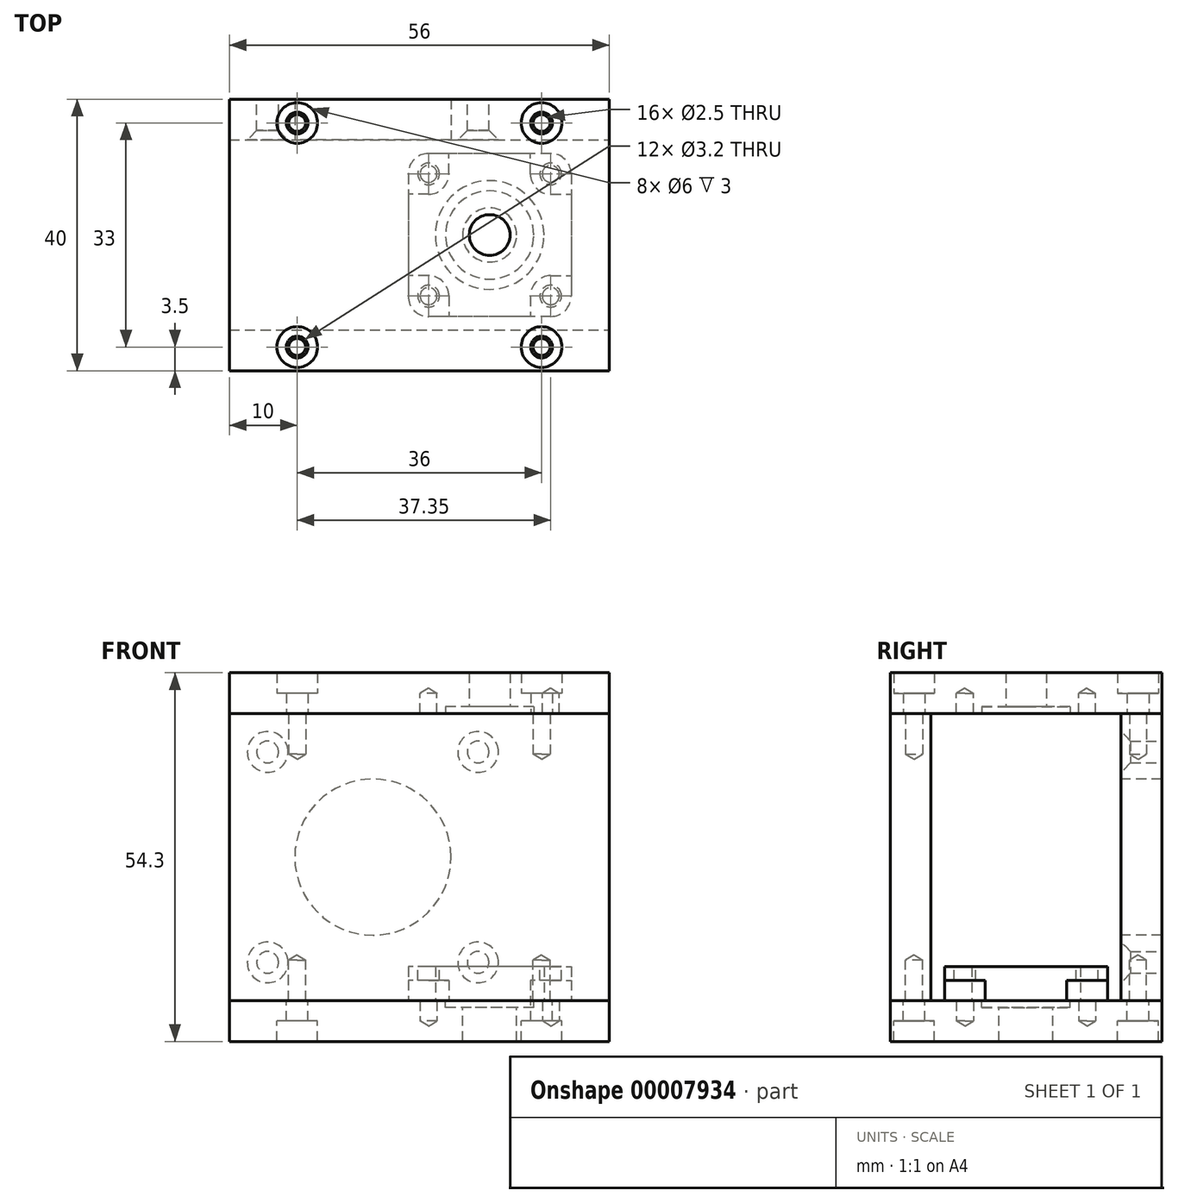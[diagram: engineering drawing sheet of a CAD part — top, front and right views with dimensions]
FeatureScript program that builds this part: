
annotation { "Feature Type Name" : "Feature", "Feature Type Description" : "" }
export const myFeature = defineFeature(function(context is Context, id is Id, definition is map)
    precondition{}
    {
        {
            var Q0;
            Q0=qCreatedBy(makeId("Top.planeOp"),FACE);
            var sketch = newSketch(context, id + "F0", { "sketchPlane" : qUnion([Q0])});
            skLineSegment(sketch, "E0.rect.bottom", {"start": v(-28, 21.15) * mm, "end": v(28, 21.15) * mm});
            skLineSegment(sketch, "E0.rect.top", {"start": v(-28, -21.15) * mm, "end": v(28, -21.15) * mm});
            skLineSegment(sketch, "E0.rect.left", {"start": v(-28, 21.15) * mm, "end": v(-28, -21.15) * mm});
            skLineSegment(sketch, "E0.rect.right", {"start": v(28, 21.15) * mm, "end": v(28, -21.15) * mm});
            skPoint(sketch, "E0.rect.middle", {"position": v(0, 0) * mm});
            skCircle(sketch, "E1", {"center": v(-6.85, 0) * mm, "radius": 11.5 * mm});
            skLineSegment(sketch, "E2", {"start": v(0, 36.49) * mm, "end": v(0, -29.8) * mm, "construction": true});
            skPoint(sketch, "E3", {"position": v(8.65, -15.5) * mm});
            skPoint(sketch, "E4", {"position": v(8.65, 15.5) * mm});
            skPoint(sketch, "E5", {"position": v(-22.35, -15.5) * mm});
            skPoint(sketch, "E6", {"position": v(-22.35, 15.5) * mm});
            skSolve(sketch);
        }
        {
            var Q0;
            Q0=makeQuery(id+"F0.imprint","IMPRINT",FACE,{"disambiguationData":[TD([[makeQuery(id+"F0.imprint","IMPRINT",EDGE,{"derivedFrom":sQuery(id+"F0.wireOp",EDGE,"E0.rect.bottom")}),-1.0]])]});
            extrude(context, id + "F1", {"entities" : qUnion([Q0]), "depth" : 6 * mm});
        }
        {
            var Q0;
            Q0=makeQuery(id+"F1.opExtrude","SWEPT_BODY",BODY,{"disambiguationData":[OSD([sQuery(id+"F0.wireOp",EDGE,"E0.rect.bottom"),sQuery(id+"F0.wireOp",EDGE,"E0.rect.top"),sQuery(id+"F0.wireOp",EDGE,"E0.rect.left"),sQuery(id+"F0.wireOp",EDGE,"E0.rect.right"),sQuery(id+"F0.wireOp",EDGE,"5d0100cf-7879-4639-aec2-40528bfa14ef"),sQuery(id+"F0.wireOp",EDGE,"8731b84f-5775-4f98-9a93-eaf35cf7c801"),sQuery(id+"F0.wireOp",EDGE,"47f3dff2-6889-448c-bae9-9e021a76fb31"),sQuery(id+"F0.wireOp",EDGE,"358dfb72-d0fd-4f4f-ac3b-25c96c6351ab"),sQuery(id+"F0.wireOp",EDGE,"E1")])]});
            var Q1;
            Q1=sQuery(id+"F0.wireOp",EDGE,"E0.rect.bottom");
            var Q2;
            Q2=sQuery(id+"F0.wireOp",EDGE,"E0.rect.bottom");
            transform(context, id + "F2", {"entities" : qUnion([Q0]), "transformType" : TransformType.ROTATION, "transformAxis" : qUnion([Q2]), "angle" : 90 * degree, "oppositeDirection" : true, "makeCopy" : false});
        }
        {
            var Q0;
            Q0=qCreatedBy(makeId("Top.planeOp"),FACE);
            var sketch = newSketch(context, id + "F3", { "sketchPlane" : qUnion([Q0])});
            skLineSegment(sketch, "E7.bottom", {"start": v(-28, 27.15) * mm, "end": v(28, 27.15) * mm});
            skLineSegment(sketch, "E7.top", {"start": v(-28, -12.85) * mm, "end": v(28, -12.85) * mm});
            skLineSegment(sketch, "E7.left", {"start": v(-28, 27.15) * mm, "end": v(-28, -12.85) * mm});
            skLineSegment(sketch, "E7.right", {"start": v(28, 27.15) * mm, "end": v(28, -12.85) * mm});
            skLineSegment(sketch, "E8", {"start": v(-6.85, 27.15) * mm, "end": v(-6.85, -12.85) * mm, "construction": true});
            skLineSegment(sketch, "E9", {"start": v(10.35, 27.15) * mm, "end": v(10.35, -12.85) * mm, "construction": true});
            skLineSegment(sketch, "E10", {"start": v(10.35, -7.18) * mm, "end": v(-6.85, -7.18) * mm, "construction": true});
            skCircle(sketch, "E11", {"center": v(10.35, 7.15) * mm, "radius": 6.5 * mm});
            skSolve(sketch);
        }
        {
            var Q0;
            Q0=makeQuery(id+"F3.imprint","IMPRINT",FACE,{"disambiguationData":[TD([[makeQuery(id+"F3.imprint","IMPRINT",EDGE,{"derivedFrom":sQuery(id+"F3.wireOp",EDGE,"E7.bottom")}),-1.0]])]});
            var Q1;
            Q1=makeQuery(id+"F3.imprint","IMPRINT",FACE,{"disambiguationData":[TD([[makeQuery(id+"F3.imprint","IMPRINT",EDGE,{"derivedFrom":sQuery(id+"F3.wireOp",EDGE,"E11")}),1.0]])]});
            extrude(context, id + "F4", {"entities" : qUnion([Q0, Q1]), "oppositeDirection" : true, "depth" : 6 * mm});
        }
        {
            var Q0;
            Q0=makeQuery(id+"F4.opExtrude","SWEPT_FACE",FACE,{"disambiguationData":[OSD([sQuery(id+"F3.wireOp",EDGE,"E7.top")])]});
            var sketch = newSketch(context, id + "F5", { "sketchPlane" : qUnion([Q0])});
            skLineSegment(sketch, "E12.bottom", {"start": v(-28, 42.3) * mm, "end": v(28, 42.3) * mm});
            skLineSegment(sketch, "E12.top", {"start": v(-28, 0) * mm, "end": v(28, 0) * mm});
            skLineSegment(sketch, "E12.left", {"start": v(28, 42.3) * mm, "end": v(28, 0) * mm});
            skLineSegment(sketch, "E12.right", {"start": v(-28, 42.3) * mm, "end": v(-28, 0) * mm});
            skSolve(sketch);
        }
        {
            var Q0;
            Q0=makeQuery(id+"F5.imprint","IMPRINT",FACE,{"disambiguationData":[TD([[makeQuery(id+"F5.imprint","IMPRINT",EDGE,{"derivedFrom":sQuery(id+"F5.wireOp",EDGE,"E12.bottom")}),-1.0]])]});
            extrude(context, id + "F6", {"entities" : qUnion([Q0]), "oppositeDirection" : true, "depth" : 6 * mm});
        }
        {
            var Q0;
            Q0=makeQuery(id+"F3.imprint","IMPRINT",FACE,{"disambiguationData":[TD([[makeQuery(id+"F3.imprint","IMPRINT",EDGE,{"derivedFrom":sQuery(id+"F3.wireOp",EDGE,"E11")}),1.0]])]});
            extrude(context, id + "F7", {"entities" : qUnion([Q0]), "operationType" : NewBodyOperationType.REMOVE, "oppositeDirection" : true, "depth" : 1 * mm});
        }
        {
            var Q0;
            Q0=makeQuery(id+"F6.opExtrude","SWEPT_FACE",FACE,{"disambiguationData":[OSD([sQuery(id+"F5.wireOp",EDGE,"E12.bottom")])]});
            var sketch = newSketch(context, id + "F8", { "sketchPlane" : qUnion([Q0])});
            skPoint(sketch, "E13.0", {"position": v(10.35, 7.15) * mm});
            skLineSegment(sketch, "E14.0", {"start": v(-28, 27.15) * mm, "end": v(28, 27.15) * mm});
            skLineSegment(sketch, "E15.0", {"start": v(28, 27.15) * mm, "end": v(28, -12.85) * mm});
            skLineSegment(sketch, "E16.0", {"start": v(-28, -12.85) * mm, "end": v(28, -12.85) * mm});
            skLineSegment(sketch, "E17.0", {"start": v(-28, 27.15) * mm, "end": v(-28, -12.85) * mm});
            skCircle(sketch, "E18", {"center": v(10.35, 7.15) * mm, "radius": 3 * mm});
            skCircle(sketch, "E19.0", {"center": v(10.35, 7.15) * mm, "radius": 6.5 * mm});
            skSolve(sketch);
        }
        {
            var Q0;
            Q0=makeQuery(id+"F8.imprint","IMPRINT",FACE,{"disambiguationData":[TD([[makeQuery(id+"F8.imprint","IMPRINT",EDGE,{"derivedFrom":sQuery(id+"F8.wireOp",EDGE,"E18")}),-1.0]])]});
            var Q1;
            {var subQ2=sQuery(id+"F8.wireOp",EDGE,"E14.0");Q1=makeQuery(id+"F8.imprint","IMPRINT",FACE,{"disambiguationData":[TD([[makeQuery(id+"F8.imprint","IMPRINT",EDGE,{"derivedFrom":subQ2}),-1.0]])]});}
            var Q2;
            {var subQ2=sQuery(id+"F8.wireOp",EDGE,"E16.0");Q2=makeQuery(id+"F8.imprint","IMPRINT",FACE,{"disambiguationData":[TD([[makeQuery(id+"F8.imprint","IMPRINT",EDGE,{"derivedFrom":subQ2}),1.0]])]});}
            extrude(context, id + "F9", {"entities" : qUnion([Q0, Q1, Q2]), "depth" : 6 * mm});
        }
        {
            var Q0;
            Q0=makeQuery(id+"F8.imprint","IMPRINT",FACE,{"disambiguationData":[TD([[makeQuery(id+"F8.imprint","IMPRINT",EDGE,{"derivedFrom":sQuery(id+"F8.wireOp",EDGE,"E18")}),-1.0]])]});
            extrude(context, id + "F10", {"entities" : qUnion([Q0]), "operationType" : NewBodyOperationType.REMOVE, "depth" : 1 * mm});
        }
        {
            var Q0;
            Q0=makeQuery(id+"F4.opExtrude","CAP_FACE",FACE,{"disambiguationData":[OSD([sQuery(id+"F3.wireOp",EDGE,"E7.bottom"),sQuery(id+"F3.wireOp",EDGE,"E7.top"),sQuery(id+"F3.wireOp",EDGE,"E7.left"),sQuery(id+"F3.wireOp",EDGE,"E7.right"),sQuery(id+"F3.wireOp",EDGE,"f328e42c-5cb5-4c08-ae33-e700e0f09d0d")])],"isStart":true});
            var sketch = newSketch(context, id + "F11", { "sketchPlane" : qUnion([Q0])});
            skCircle(sketch, "E20", {"center": v(19.35, -1.85) * mm, "radius": 3 * mm});
            skCircle(sketch, "E21", {"center": v(1.35, 16.15) * mm, "radius": 3 * mm});
            skCircle(sketch, "E22", {"center": v(19.35, 16.15) * mm, "radius": 3 * mm});
            skCircle(sketch, "E23", {"center": v(1.35, -1.85) * mm, "radius": 3 * mm});
            skLineSegment(sketch, "E24", {"start": v(19.35, -1.85) * mm, "end": v(22.35, -1.85) * mm, "construction": true});
            skLineSegment(sketch, "E25", {"start": v(19.35, -1.85) * mm, "end": v(19.35, -4.85) * mm, "construction": true});
            skPoint(sketch, "E26.0", {"position": v(10.35, 7.15) * mm});
            skCircle(sketch, "E27", {"center": v(10.35, 7.15) * mm, "radius": 8 * mm});
            skLineSegment(sketch, "E28.rect.bottom", {"start": v(22.35, 19.15) * mm, "end": v(-1.65, 19.15) * mm});
            skLineSegment(sketch, "E28.rect.top", {"start": v(22.35, -4.85) * mm, "end": v(-1.65, -4.85) * mm});
            skLineSegment(sketch, "E28.rect.left", {"start": v(22.35, 19.15) * mm, "end": v(22.35, -4.85) * mm});
            skLineSegment(sketch, "E28.rect.right", {"start": v(-1.65, 19.15) * mm, "end": v(-1.65, -4.85) * mm});
            skLineSegment(sketch, "E29", {"start": v(1.35, 13.15) * mm, "end": v(-1.65, 13.15) * mm});
            skLineSegment(sketch, "E30", {"start": v(22.35, 7.15) * mm, "end": v(-1.65, 7.15) * mm, "construction": true});
            skLineSegment(sketch, "E31", {"start": v(10.35, 19.15) * mm, "end": v(10.35, -4.85) * mm, "construction": true});
            skLineSegment(sketch, "E32", {"start": v(4.35, 16.15) * mm, "end": v(4.35, 19.15) * mm});
            skLineSegment(sketch, "E33", {"start": v(4.35, -1.85) * mm, "end": v(4.35, -4.85) * mm});
            skLineSegment(sketch, "E34", {"start": v(1.35, 1.15) * mm, "end": v(-1.65, 1.15) * mm});
            skLineSegment(sketch, "E35", {"start": v(16.35, 16.15) * mm, "end": v(16.35, 19.15) * mm});
            skLineSegment(sketch, "E36", {"start": v(19.35, 13.15) * mm, "end": v(22.35, 13.15) * mm});
            skLineSegment(sketch, "E37", {"start": v(16.35, -1.85) * mm, "end": v(16.35, -4.85) * mm});
            skLineSegment(sketch, "E38", {"start": v(19.35, 1.15) * mm, "end": v(22.35, 1.15) * mm});
            skSolve(sketch);
        }
        {
            var Q0;
            Q0=makeQuery(id+"F11.imprint","IMPRINT",FACE,{"disambiguationData":[TD([[makeQuery(id+"F11.imprint","IMPRINT",EDGE,{"derivedFrom":sQuery(id+"F11.wireOp",EDGE,"E27")}),-1.0]])]});
            var Q1;
            {var subQ0=sQuery(id+"F11.wireOp",EDGE,"E23");var subQ2=makeQuery(id+"F11.imprint","INTERSECT",VERTEX,{"derivedFrom":[subQ0,sQuery(id+"F11.wireOp",EDGE,"E33")]});Q1=makeQuery(id+"F11.imprint","IMPRINT",FACE,{"disambiguationData":[TD([[makeQuery(id+"F11.imprint","IMPRINT",EDGE,{"disambiguationData":[TD([[subQ2,-1.0]])],"derivedFrom":subQ0}),1.0]])]});}
            var Q2;
            {var subQ0=sQuery(id+"F11.wireOp",EDGE,"E34");Q2=makeQuery(id+"F11.imprint","IMPRINT",FACE,{"disambiguationData":[TD([[makeQuery(id+"F11.imprint","IMPRINT",EDGE,{"derivedFrom":subQ0}),1.0]])]});}
            var Q3;
            {var subQ0=sQuery(id+"F11.wireOp",EDGE,"E33");Q3=makeQuery(id+"F11.imprint","IMPRINT",FACE,{"disambiguationData":[TD([[makeQuery(id+"F11.imprint","IMPRINT",EDGE,{"derivedFrom":subQ0}),-1.0]])]});}
            var Q4;
            {var subQ0=sQuery(id+"F11.wireOp",EDGE,"E32");Q4=makeQuery(id+"F11.imprint","IMPRINT",FACE,{"disambiguationData":[TD([[makeQuery(id+"F11.imprint","IMPRINT",EDGE,{"derivedFrom":subQ0}),1.0]])]});}
            var Q5;
            {var subQ0=sQuery(id+"F11.wireOp",EDGE,"E21");var subQ4=makeQuery(id+"F11.imprint","INTERSECT",VERTEX,{"derivedFrom":[subQ0,sQuery(id+"F11.wireOp",EDGE,"E28.rect.right")]});Q5=makeQuery(id+"F11.imprint","IMPRINT",FACE,{"disambiguationData":[TD([[makeQuery(id+"F11.imprint","IMPRINT",EDGE,{"disambiguationData":[TD([[subQ4,1.0]])],"derivedFrom":subQ0}),1.0]])]});}
            var Q6;
            {var subQ0=sQuery(id+"F11.wireOp",EDGE,"E29");Q6=makeQuery(id+"F11.imprint","IMPRINT",FACE,{"disambiguationData":[TD([[makeQuery(id+"F11.imprint","IMPRINT",EDGE,{"derivedFrom":subQ0}),-1.0]])]});}
            var Q7;
            {var subQ3=sQuery(id+"F11.wireOp",EDGE,"E35");Q7=makeQuery(id+"F11.imprint","IMPRINT",FACE,{"disambiguationData":[TD([[makeQuery(id+"F11.imprint","IMPRINT",EDGE,{"derivedFrom":subQ3}),-1.0]])]});}
            var Q8;
            {var subQ0=sQuery(id+"F11.wireOp",EDGE,"E22");var subQ4=makeQuery(id+"F11.imprint","INTERSECT",VERTEX,{"derivedFrom":[subQ0,sQuery(id+"F11.wireOp",EDGE,"E35")]});Q8=makeQuery(id+"F11.imprint","IMPRINT",FACE,{"disambiguationData":[TD([[makeQuery(id+"F11.imprint","IMPRINT",EDGE,{"disambiguationData":[TD([[subQ4,1.0]])],"derivedFrom":subQ0}),1.0]])]});}
            var Q9;
            {var subQ0=sQuery(id+"F11.wireOp",EDGE,"E36");Q9=makeQuery(id+"F11.imprint","IMPRINT",FACE,{"disambiguationData":[TD([[makeQuery(id+"F11.imprint","IMPRINT",EDGE,{"derivedFrom":subQ0}),1.0]])]});}
            var Q10;
            {var subQ0=sQuery(id+"F11.wireOp",EDGE,"E38");Q10=makeQuery(id+"F11.imprint","IMPRINT",FACE,{"disambiguationData":[TD([[makeQuery(id+"F11.imprint","IMPRINT",EDGE,{"derivedFrom":subQ0}),-1.0]])]});}
            var Q11;
            {var subQ0=sQuery(id+"F11.wireOp",EDGE,"E20");var subQ4=makeQuery(id+"F11.imprint","INTERSECT",VERTEX,{"derivedFrom":[subQ0,sQuery(id+"F11.wireOp",EDGE,"E38")]});Q11=makeQuery(id+"F11.imprint","IMPRINT",FACE,{"disambiguationData":[TD([[makeQuery(id+"F11.imprint","IMPRINT",EDGE,{"disambiguationData":[TD([[subQ4,1.0]])],"derivedFrom":subQ0}),1.0]])]});}
            var Q12;
            {var subQ0=sQuery(id+"F11.wireOp",EDGE,"E37");Q12=makeQuery(id+"F11.imprint","IMPRINT",FACE,{"disambiguationData":[TD([[makeQuery(id+"F11.imprint","IMPRINT",EDGE,{"derivedFrom":subQ0}),1.0]])]});}
            extrude(context, id + "F12", {"entities" : qUnion([Q0, Q1, Q2, Q3, Q4, Q5, Q6, Q7, Q8, Q9, Q10, Q11, Q12]), "depth" : 5 * mm});
        }
        {
            var Q0;
            Q0=sQuery(id+"F11.wireOp",VERTEX,"E21.center");
            var Q1;
            Q1=sQuery(id+"F11.wireOp",VERTEX,"E23.center");
            var Q2;
            Q2=sQuery(id+"F11.wireOp",VERTEX,"E20.center");
            var Q3;
            Q3=sQuery(id+"F11.wireOp",VERTEX,"E22.center");
            var Q4;
            Q4=makeQuery(id+"F12.opExtrude","SWEPT_BODY",BODY,{"disambiguationData":[OSD([sQuery(id+"F11.wireOp",EDGE,"E20"),sQuery(id+"F11.wireOp",EDGE,"E21"),sQuery(id+"F11.wireOp",EDGE,"E22"),sQuery(id+"F11.wireOp",EDGE,"E23"),sQuery(id+"F11.wireOp",EDGE,"E27"),sQuery(id+"F11.wireOp",EDGE,"E28.rect.bottom"),sQuery(id+"F11.wireOp",EDGE,"E28.rect.top"),sQuery(id+"F11.wireOp",EDGE,"E28.rect.left"),sQuery(id+"F11.wireOp",EDGE,"E28.rect.right")])]});
            hole(context, id + "F13", {"style" : HoleStyle.C_BORE, "holeDiameter" : 3.2 * mm, "cBoreDiameter" : 6 * mm, "cBoreDepth" : 3 * mm, "endStyle" : HoleEndStyle.THROUGH, "oppositeDirection" : true, "locations" : qUnion([Q0, Q1, Q2, Q3]), "scope" : qUnion([Q4])});
        }
        {
            var Q0;
            {var subQ0=sQuery(id+"F11.wireOp",EDGE,"E34");Q0=makeQuery(id+"F11.imprint","IMPRINT",FACE,{"disambiguationData":[TD([[makeQuery(id+"F11.imprint","IMPRINT",EDGE,{"derivedFrom":subQ0}),1.0]])]});}
            var Q1;
            {var subQ0=sQuery(id+"F11.wireOp",EDGE,"E29");Q1=makeQuery(id+"F11.imprint","IMPRINT",FACE,{"disambiguationData":[TD([[makeQuery(id+"F11.imprint","IMPRINT",EDGE,{"derivedFrom":subQ0}),-1.0]])]});}
            var Q2;
            {var subQ0=sQuery(id+"F11.wireOp",EDGE,"E32");Q2=makeQuery(id+"F11.imprint","IMPRINT",FACE,{"disambiguationData":[TD([[makeQuery(id+"F11.imprint","IMPRINT",EDGE,{"derivedFrom":subQ0}),1.0]])]});}
            var Q3;
            {var subQ3=sQuery(id+"F11.wireOp",EDGE,"E35");Q3=makeQuery(id+"F11.imprint","IMPRINT",FACE,{"disambiguationData":[TD([[makeQuery(id+"F11.imprint","IMPRINT",EDGE,{"derivedFrom":subQ3}),-1.0]])]});}
            var Q4;
            {var subQ0=sQuery(id+"F11.wireOp",EDGE,"E36");Q4=makeQuery(id+"F11.imprint","IMPRINT",FACE,{"disambiguationData":[TD([[makeQuery(id+"F11.imprint","IMPRINT",EDGE,{"derivedFrom":subQ0}),1.0]])]});}
            var Q5;
            {var subQ0=sQuery(id+"F11.wireOp",EDGE,"E38");Q5=makeQuery(id+"F11.imprint","IMPRINT",FACE,{"disambiguationData":[TD([[makeQuery(id+"F11.imprint","IMPRINT",EDGE,{"derivedFrom":subQ0}),-1.0]])]});}
            var Q6;
            {var subQ0=sQuery(id+"F11.wireOp",EDGE,"E37");Q6=makeQuery(id+"F11.imprint","IMPRINT",FACE,{"disambiguationData":[TD([[makeQuery(id+"F11.imprint","IMPRINT",EDGE,{"derivedFrom":subQ0}),1.0]])]});}
            var Q7;
            {var subQ0=sQuery(id+"F11.wireOp",EDGE,"E33");Q7=makeQuery(id+"F11.imprint","IMPRINT",FACE,{"disambiguationData":[TD([[makeQuery(id+"F11.imprint","IMPRINT",EDGE,{"derivedFrom":subQ0}),-1.0]])]});}
            extrude(context, id + "F14", {"entities" : qUnion([Q0, Q1, Q2, Q3, Q4, Q5, Q6, Q7]), "operationType" : NewBodyOperationType.REMOVE, "depth" : 3 * mm});
        }
        {
            var Q0;
            Q0=makeQuery(id+"F4.opExtrude","CAP_FACE",FACE,{"disambiguationData":[OSD([sQuery(id+"F3.wireOp",EDGE,"E7.bottom"),sQuery(id+"F3.wireOp",EDGE,"E7.top"),sQuery(id+"F3.wireOp",EDGE,"E7.left"),sQuery(id+"F3.wireOp",EDGE,"E7.right")])],"isStart":false});
            var sketch = newSketch(context, id + "F15", { "sketchPlane" : qUnion([Q0])});
            skPoint(sketch, "E39.0", {"position": v(-18, -23.65) * mm});
            skPoint(sketch, "E40.0", {"position": v(18, -23.65) * mm});
            skPoint(sketch, "E41.0", {"position": v(18, 9.35) * mm});
            skPoint(sketch, "E42.0", {"position": v(-18, 9.35) * mm});
            skLineSegment(sketch, "E43", {"start": v(18, 9.35) * mm, "end": v(28, 9.35) * mm, "construction": true});
            skLineSegment(sketch, "E44", {"start": v(18, 9.35) * mm, "end": v(18, 12.85) * mm, "construction": true});
            skLineSegment(sketch, "E45", {"start": v(-18, 9.35) * mm, "end": v(-18, 12.85) * mm, "construction": true});
            skLineSegment(sketch, "E46", {"start": v(-18, 9.35) * mm, "end": v(-28, 9.35) * mm, "construction": true});
            skLineSegment(sketch, "E47", {"start": v(-18, -23.65) * mm, "end": v(-18, -27.15) * mm, "construction": true});
            skLineSegment(sketch, "E48", {"start": v(-18, -23.65) * mm, "end": v(-28, -23.65) * mm, "construction": true});
            skLineSegment(sketch, "E49", {"start": v(18, -23.65) * mm, "end": v(28, -23.65) * mm, "construction": true});
            skLineSegment(sketch, "E50", {"start": v(18, -23.65) * mm, "end": v(18, -27.15) * mm, "construction": true});
            skLineSegment(sketch, "E51", {"start": v(0, 12.85) * mm, "end": v(0, -27.15) * mm, "construction": true});
            skLineSegment(sketch, "E52", {"start": v(-28, -7.15) * mm, "end": v(0, -7.15) * mm, "construction": true});
            skPoint(sketch, "E53", {"position": v(20, -17.15) * mm});
            skPoint(sketch, "E54", {"position": v(-20, -17.15) * mm});
            skPoint(sketch, "E55", {"position": v(-20, 2.85) * mm});
            skPoint(sketch, "E56", {"position": v(20, 2.85) * mm});
            skCircle(sketch, "E57.0", {"center": v(10.35, -7.15) * mm, "radius": 3 * mm});
            skSolve(sketch);
        }
        {
            var Q0;
            Q0=makeQuery(id+"F9.opExtrude","CAP_FACE",FACE,{"disambiguationData":[OSD([sQuery(id+"F8.wireOp",EDGE,"E14.0"),sQuery(id+"F8.wireOp",EDGE,"E15.0"),sQuery(id+"F8.wireOp",EDGE,"E16.0"),sQuery(id+"F8.wireOp",EDGE,"E17.0"),sQuery(id+"F8.wireOp",EDGE,"E18")])],"isStart":false});
            var sketch = newSketch(context, id + "F16", { "sketchPlane" : qUnion([Q0])});
            skPoint(sketch, "E58.0", {"position": v(18, 23.65) * mm});
            skPoint(sketch, "E59.0", {"position": v(-18, 23.65) * mm});
            skPoint(sketch, "E60.0", {"position": v(18, -9.35) * mm});
            skPoint(sketch, "E61.0", {"position": v(-18, -9.35) * mm});
            skSolve(sketch);
        }
        {
            var Q0;
            Q0=sQuery(id+"F15.wireOp",VERTEX,"E39.0");
            var Q1;
            Q1=sQuery(id+"F15.wireOp",VERTEX,"E42.0");
            var Q2;
            Q2=sQuery(id+"F15.wireOp",VERTEX,"E41.0");
            var Q3;
            Q3=sQuery(id+"F15.wireOp",VERTEX,"E40.0");
            var Q4;
            Q4=sQuery(id+"F16.wireOp",VERTEX,"E61.0");
            var Q5;
            Q5=sQuery(id+"F16.wireOp",VERTEX,"E59.0");
            var Q6;
            Q6=sQuery(id+"F16.wireOp",VERTEX,"E58.0");
            var Q7;
            Q7=sQuery(id+"F16.wireOp",VERTEX,"E60.0");
            var Q8;
            Q8=makeQuery(id+"F4.opExtrude","SWEPT_BODY",BODY,{"disambiguationData":[OSD([sQuery(id+"F3.wireOp",EDGE,"E7.bottom"),sQuery(id+"F3.wireOp",EDGE,"E7.top"),sQuery(id+"F3.wireOp",EDGE,"E7.left"),sQuery(id+"F3.wireOp",EDGE,"E7.right")])]});
            var Q9;
            Q9=makeQuery(id+"F9.opExtrude","SWEPT_BODY",BODY,{"disambiguationData":[OSD([sQuery(id+"F8.wireOp",EDGE,"E14.0"),sQuery(id+"F8.wireOp",EDGE,"E15.0"),sQuery(id+"F8.wireOp",EDGE,"E16.0"),sQuery(id+"F8.wireOp",EDGE,"E17.0"),sQuery(id+"F8.wireOp",EDGE,"E18")])]});
            hole(context, id + "F17", {"style" : HoleStyle.C_BORE, "holeDiameter" : 3.2 * mm, "cBoreDiameter" : 6 * mm, "cBoreDepth" : 3 * mm, "endStyle" : HoleEndStyle.BLIND, "holeDepth" : 6 * mm, "locations" : qUnion([Q0, Q1, Q2, Q3, Q4, Q5, Q6, Q7]), "scope" : qUnion([Q8, Q9])});
        }
        {
            var Q0;
            Q0=makeQuery(id+"F1.opExtrude","SWEPT_FACE",FACE,{"disambiguationData":[OSD([sQuery(id+"F0.wireOp",EDGE,"E0.rect.top")])]});
            var sketch = newSketch(context, id + "F18", { "sketchPlane" : qUnion([Q0])});
            skPoint(sketch, "E62.0", {"position": v(-18, 23.65) * mm});
            skPoint(sketch, "E63.0", {"position": v(18, 23.65) * mm});
            skPoint(sketch, "E64.0", {"position": v(-18, -9.35) * mm});
            skPoint(sketch, "E65.0", {"position": v(18, -9.35) * mm});
            skSolve(sketch);
        }
        {
            var Q0;
            Q0=makeQuery(id+"F6.opExtrude","SWEPT_FACE",FACE,{"disambiguationData":[OSD([sQuery(id+"F5.wireOp",EDGE,"E12.top")])]});
            var sketch = newSketch(context, id + "F19", { "sketchPlane" : qUnion([Q0])});
            skPoint(sketch, "E66.0", {"position": v(-18, -23.65) * mm});
            skPoint(sketch, "E67.0", {"position": v(18, -23.65) * mm});
            skPoint(sketch, "E68.0", {"position": v(18, 9.35) * mm});
            skPoint(sketch, "E69.0", {"position": v(-18, 9.35) * mm});
            skSolve(sketch);
        }
        {
            var Q0;
            Q0=sQuery(id+"F18.wireOp",VERTEX,"E62.0");
            var Q1;
            Q1=sQuery(id+"F18.wireOp",VERTEX,"E63.0");
            var Q2;
            Q2=sQuery(id+"F18.wireOp",VERTEX,"E64.0");
            var Q3;
            Q3=sQuery(id+"F18.wireOp",VERTEX,"E65.0");
            var Q4;
            Q4=sQuery(id+"F19.wireOp",VERTEX,"E66.0");
            var Q5;
            Q5=sQuery(id+"F19.wireOp",VERTEX,"E67.0");
            var Q6;
            Q6=sQuery(id+"F19.wireOp",VERTEX,"E69.0");
            var Q7;
            Q7=sQuery(id+"F19.wireOp",VERTEX,"E68.0");
            var Q8;
            Q8=makeQuery(id+"F6.opExtrude","SWEPT_BODY",BODY,{"disambiguationData":[OSD([sQuery(id+"F5.wireOp",EDGE,"E12.bottom"),sQuery(id+"F5.wireOp",EDGE,"E12.top"),sQuery(id+"F5.wireOp",EDGE,"E12.left"),sQuery(id+"F5.wireOp",EDGE,"E12.right")])]});
            var Q9;
            Q9=makeQuery(id+"F1.opExtrude","SWEPT_BODY",BODY,{"disambiguationData":[OSD([sQuery(id+"F0.wireOp",EDGE,"E0.rect.bottom"),sQuery(id+"F0.wireOp",EDGE,"E0.rect.top"),sQuery(id+"F0.wireOp",EDGE,"E0.rect.left"),sQuery(id+"F0.wireOp",EDGE,"E0.rect.right"),sQuery(id+"F0.wireOp",EDGE,"5d0100cf-7879-4639-aec2-40528bfa14ef"),sQuery(id+"F0.wireOp",EDGE,"8731b84f-5775-4f98-9a93-eaf35cf7c801"),sQuery(id+"F0.wireOp",EDGE,"47f3dff2-6889-448c-bae9-9e021a76fb31"),sQuery(id+"F0.wireOp",EDGE,"358dfb72-d0fd-4f4f-ac3b-25c96c6351ab"),sQuery(id+"F0.wireOp",EDGE,"E1")])]});
            hole(context, id + "F20", {"style" : HoleStyle.SIMPLE, "holeDiameter" : 2.5 * mm, "endStyle" : HoleEndStyle.BLIND, "holeDepth" : 6 * mm, "locations" : qUnion([Q0, Q1, Q2, Q3, Q4, Q5, Q6, Q7]), "scope" : qUnion([Q8, Q9])});
        }
        {
            var Q0;
            Q0=makeQuery(id+"F9.opExtrude","CAP_FACE",FACE,{"disambiguationData":[OSD([sQuery(id+"F8.wireOp",EDGE,"E14.0"),sQuery(id+"F8.wireOp",EDGE,"E15.0"),sQuery(id+"F8.wireOp",EDGE,"E16.0"),sQuery(id+"F8.wireOp",EDGE,"E17.0"),sQuery(id+"F8.wireOp",EDGE,"E18")])],"isStart":true});
            var sketch = newSketch(context, id + "F21", { "sketchPlane" : qUnion([Q0])});
            skPoint(sketch, "E70.0", {"position": v(19.35, -16.15) * mm});
            skPoint(sketch, "E71.0", {"position": v(1.35, -16.15) * mm});
            skPoint(sketch, "E72.0", {"position": v(19.35, 1.85) * mm});
            skPoint(sketch, "E73.0", {"position": v(1.35, 1.85) * mm});
            skSolve(sketch);
        }
        {
            var Q0;
            Q0=sQuery(id+"F11.wireOp",VERTEX,"E20.center");
            var Q1;
            Q1=sQuery(id+"F11.wireOp",VERTEX,"E23.center");
            var Q2;
            Q2=sQuery(id+"F11.wireOp",VERTEX,"E22.center");
            var Q3;
            Q3=sQuery(id+"F11.wireOp",VERTEX,"E21.center");
            var Q4;
            Q4=sQuery(id+"F21.wireOp",VERTEX,"E73.0");
            var Q5;
            Q5=sQuery(id+"F21.wireOp",VERTEX,"E71.0");
            var Q6;
            Q6=sQuery(id+"F21.wireOp",VERTEX,"E72.0");
            var Q7;
            Q7=sQuery(id+"F21.wireOp",VERTEX,"E70.0");
            var Q8;
            Q8=makeQuery(id+"F4.opExtrude","SWEPT_BODY",BODY,{"disambiguationData":[OSD([sQuery(id+"F3.wireOp",EDGE,"E7.bottom"),sQuery(id+"F3.wireOp",EDGE,"E7.top"),sQuery(id+"F3.wireOp",EDGE,"E7.left"),sQuery(id+"F3.wireOp",EDGE,"E7.right")])]});
            var Q9;
            Q9=makeQuery(id+"F9.opExtrude","SWEPT_BODY",BODY,{"disambiguationData":[OSD([sQuery(id+"F8.wireOp",EDGE,"E14.0"),sQuery(id+"F8.wireOp",EDGE,"E15.0"),sQuery(id+"F8.wireOp",EDGE,"E16.0"),sQuery(id+"F8.wireOp",EDGE,"E17.0"),sQuery(id+"F8.wireOp",EDGE,"E18")])]});
            hole(context, id + "F22", {"style" : HoleStyle.SIMPLE, "holeDiameter" : 2.5 * mm, "endStyle" : HoleEndStyle.BLIND, "holeDepth" : 3 * mm, "locations" : qUnion([Q0, Q1, Q2, Q3, Q4, Q5, Q6, Q7]), "scope" : qUnion([Q8, Q9])});
        }
        {
            var Q0;
            Q0=sQuery(id+"F15.wireOp",VERTEX,"E57.0.center");
            var Q1;
            Q1=makeQuery(id+"F4.opExtrude","SWEPT_BODY",BODY,{"disambiguationData":[OSD([sQuery(id+"F3.wireOp",EDGE,"E7.bottom"),sQuery(id+"F3.wireOp",EDGE,"E7.top"),sQuery(id+"F3.wireOp",EDGE,"E7.left"),sQuery(id+"F3.wireOp",EDGE,"E7.right")])]});
            hole(context, id + "F23", {"style" : HoleStyle.SIMPLE, "holeDiameter" : 7.95 * mm, "endStyle" : HoleEndStyle.THROUGH, "locations" : qUnion([Q0]), "scope" : qUnion([Q1])});
        }
        {
            var Q0;
            Q0=makeQuery(id+"F1.opExtrude","CAP_FACE",FACE,{"disambiguationData":[OSD([sQuery(id+"F0.wireOp",EDGE,"E0.rect.bottom"),sQuery(id+"F0.wireOp",EDGE,"E0.rect.top"),sQuery(id+"F0.wireOp",EDGE,"E0.rect.left"),sQuery(id+"F0.wireOp",EDGE,"E0.rect.right"),sQuery(id+"F0.wireOp",EDGE,"E1")])],"isStart":true});
            var sketch = newSketch(context, id + "F24", { "sketchPlane" : qUnion([Q0])});
            skLineSegment(sketch, "E74", {"start": v(-6.85, 21.15) * mm, "end": v(-6.85, 42.36) * mm, "construction": true});
            skLineSegment(sketch, "E75", {"start": v(-6.85, 21.15) * mm, "end": v(-28.67, 21.15) * mm, "construction": true});
            skPoint(sketch, "E76", {"position": v(-22.35, 36.65) * mm});
            skPoint(sketch, "E77", {"position": v(8.65, 36.65) * mm});
            skPoint(sketch, "E78", {"position": v(-22.35, 5.65) * mm});
            skPoint(sketch, "E79", {"position": v(8.65, 5.65) * mm});
            skSolve(sketch);
        }
        {
            var Q0;
            Q0=sQuery(id+"F24.wireOp",VERTEX,"E76");
            var Q1;
            Q1=sQuery(id+"F24.wireOp",VERTEX,"E77");
            var Q2;
            Q2=sQuery(id+"F24.wireOp",VERTEX,"E78");
            var Q3;
            Q3=sQuery(id+"F24.wireOp",VERTEX,"E79");
            var Q4;
            Q4=makeQuery(id+"F1.opExtrude","SWEPT_BODY",BODY,{"disambiguationData":[OSD([sQuery(id+"F0.wireOp",EDGE,"E0.rect.bottom"),sQuery(id+"F0.wireOp",EDGE,"E0.rect.top"),sQuery(id+"F0.wireOp",EDGE,"E0.rect.left"),sQuery(id+"F0.wireOp",EDGE,"E0.rect.right"),sQuery(id+"F0.wireOp",EDGE,"E1")])]});
            hole(context, id + "F25", {"style" : HoleStyle.C_SINK, "holeDiameter" : 3.2 * mm, "cSinkDiameter" : 6 * mm, "endStyle" : HoleEndStyle.THROUGH, "locations" : qUnion([Q0, Q1, Q2, Q3]), "scope" : qUnion([Q4]), "cSinkAngle" : 90 * degree});
        }
    });
